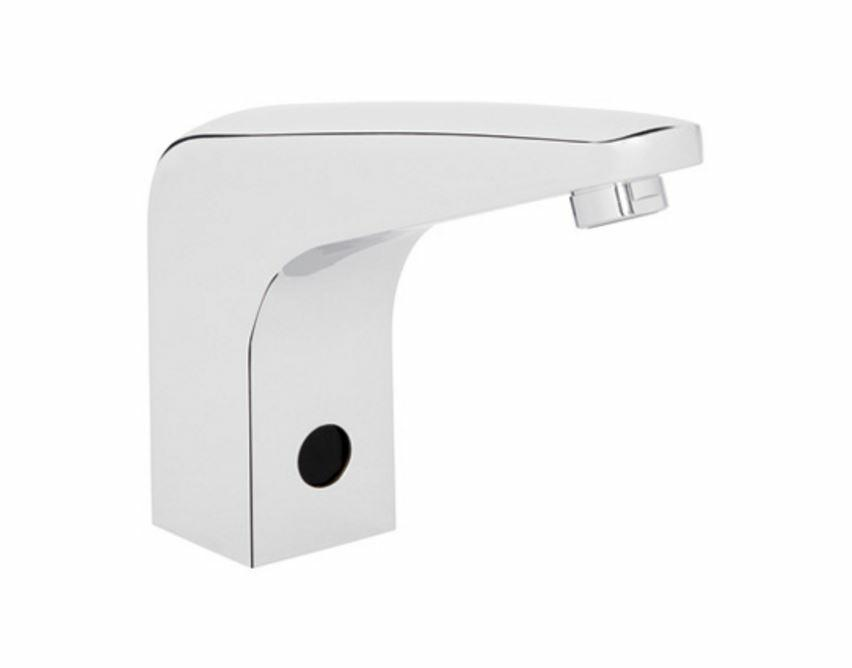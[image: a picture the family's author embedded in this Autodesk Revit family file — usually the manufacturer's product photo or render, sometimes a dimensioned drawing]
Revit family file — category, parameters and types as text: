
# Revit family: TV304-C-1.5
name_source: partatom
category: Aparatos sanitarios
units: mm (PartAtom-declared; Revit-internal decimal feet)

## family parameters
Compartido = Sí
Corte con vacíos al cargar = No
Cota de conector redondo = Diámetro de uso
Número OmniClass = 23.45.55.14
Punto de cálculo de habitación = Sí
Se basa en plano de trabajo = No
Siempre vertical = Sí
Tipo de pieza = Normal
Título OmniClass = Single Faucets

## types (1)
- TV304-C-1.5
    Accesorios = Llave hexagonal 1-1/16", Kit de sujeción, Módulo electrónico
    Chrome = Brass Chromed
    Comentarios de tipo = Línea Electrónica
    Conexión AF = Sí
    Connection = ½" - 14 NPSM
    Descripción = Llave electrónica de sensor de corriente.
    Detection Range = 9.8" (25 cm)
    Elevación por defecto = 0 "
    Fabricante = Helvex
    Features = Sensor infrarrojo, Distancia de detección 25cm (ajuste de fábrica), Fuente de alimentación regulada clase 2, Entrada: 115 - 230 Vca, 50/60 Hz, Salida: 6V cc/200mA
    Feeding Voltage = 6 V
    Imagen de tipo = TV-304.JPG
    Max. Working Pressure = 85.3 psi
    Min. Working Pressure = 5.6 psi
    Modelo = TV304-C-1.5
    Operación = Active la salida colocando su mano dentro de la
zona de detección.

## geometry (parser evidence)
native form markers: Sweep x3
no freeform markers — native parametric forms only
